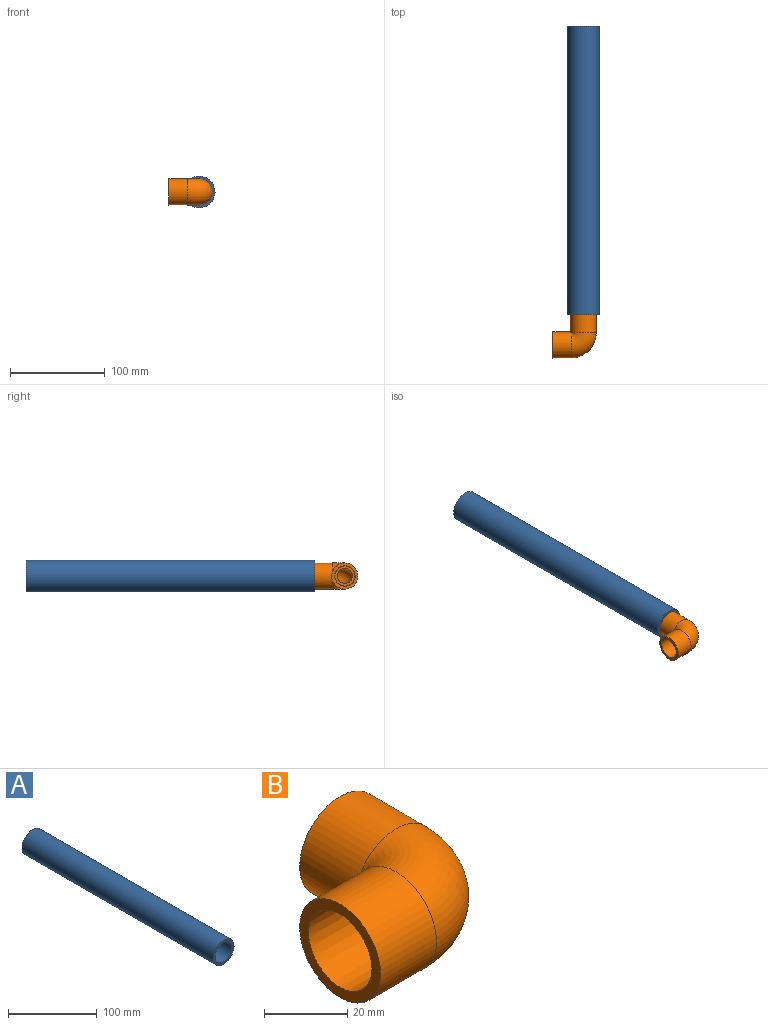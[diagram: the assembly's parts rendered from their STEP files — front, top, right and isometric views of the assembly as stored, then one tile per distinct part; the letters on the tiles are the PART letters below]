
ASSEMBLY  parts=2 mates=1
PART A: 4 faces, bbox 33.4x304x33.4 mm
  f0: cylinder r=13.32mm len=304mm, axis (0,1,0), area 25446.8mm2, adj f2,f3
  f1: cylinder r=16.7mm len=304mm, axis (0,1,0), area 31899.4mm2, adj f2,f3
  f2: plane 33.4x33.4mm, normal (0,-1,0), area 318.6mm2, adj f0,f1
  f3: plane 33.4x33.4mm, normal (0,1,0), area 318.6mm2, adj f0,f1
PART B: 10 faces, bbox 45.5x45.5x27.6 mm
  f0: torus R=12.7mm, axis (0,0,-1), area 990.1mm2, adj f7,f8
  f1: cone r=10.77mm half-angle=0.5deg, axis (0,1,0), area 1280mm2, adj f7,f9
  f2: cylinder r=13.78mm len=27.56mm, axis (0,-1,0), area 1641.5mm2, adj f3,f6,f9
  f3: cylinder r=13.78mm len=27.56mm, axis (-1,0,0), area 1641.5mm2, adj f2,f5,f6
  f4: cone r=10.62mm half-angle=0.5deg, axis (-1,0,0), area 1280mm2, adj f5,f8
  f5: plane 27.56x27.56mm, normal (-1,0,0), area 232.1mm2, adj f3,f4
  f6: torus R=12.7mm, axis (0,0,-1), area 1739.5mm2, adj f2,f3
  f7: plane 21.23x21.23mm, normal (0,1,0), area 158.1mm2, adj f0,f1
  f8: plane 21.23x21.23mm, normal (-1,0,0), area 158.1mm2, adj f0,f4
  f9: plane 27.56x27.56mm, normal (0,1,0), area 232.1mm2, adj f1,f2
PLACE A t=(-417.48,202.86,183.47)mm
PLACE B t=(-417.48,-132.89,183.47)mm
MATE fastened A.f0 <-> B.f1  axis (0,-1,0) through (-417.48,-101.14,183.47)mm
